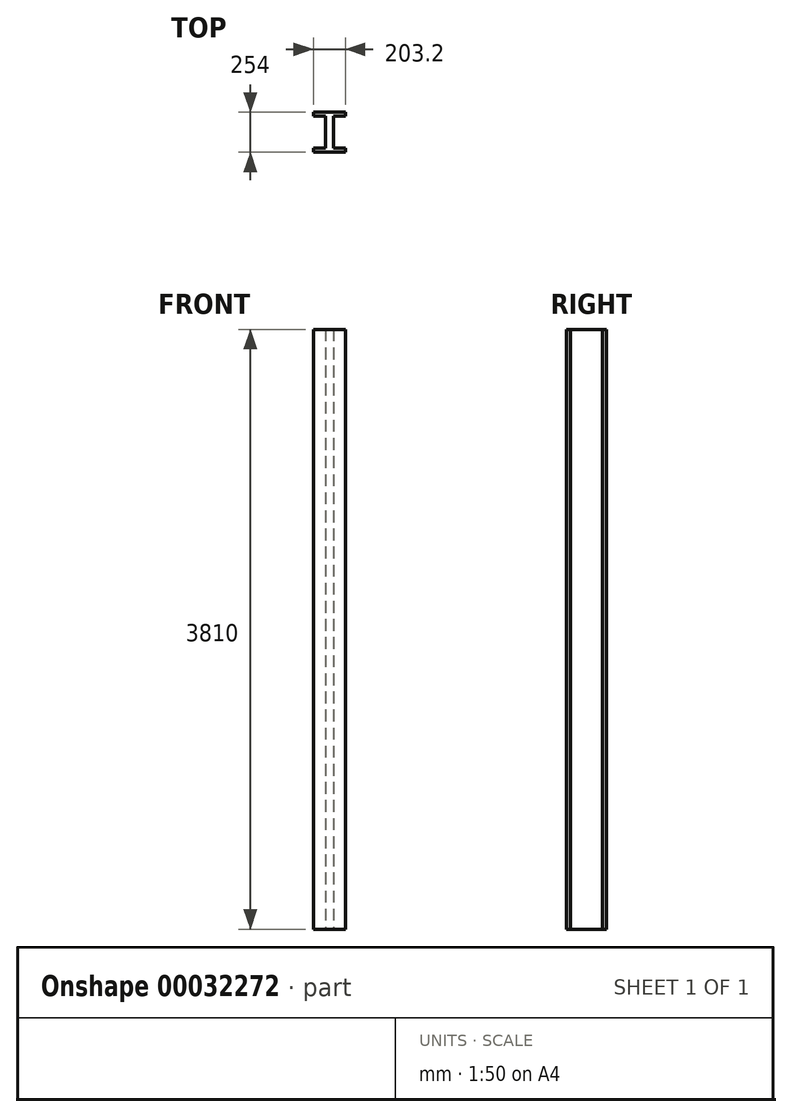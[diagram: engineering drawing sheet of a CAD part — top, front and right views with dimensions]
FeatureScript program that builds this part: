
annotation { "Feature Type Name" : "Feature", "Feature Type Description" : "" }
export const myFeature = defineFeature(function(context is Context, id is Id, definition is map)
    precondition{}
    {
        {
            var Q0;
            Q0=qCreatedBy(makeId("Top.planeOp"),FACE);
            var sketch = newSketch(context, id + "F0", { "sketchPlane" : qUnion([Q0])});
            skLineSegment(sketch, "E0.bottom", {"start": v(0, 0) * mm, "end": v(-203.2, 0) * mm});
            skLineSegment(sketch, "E0.top", {"start": v(0, -254) * mm, "end": v(-203.2, -254) * mm});
            skLineSegment(sketch, "E0.left", {"start": v(0, 0) * mm, "end": v(0, -25.4) * mm});
            skLineSegment(sketch, "E0.right", {"start": v(-203.2, 0) * mm, "end": v(-203.2, -25.4) * mm});
            skLineSegment(sketch, "E1.bottom", {"start": v(-203.2, -25.4) * mm, "end": v(-127, -25.4) * mm});
            skLineSegment(sketch, "E1.top", {"start": v(-203.2, -228.6) * mm, "end": v(-127, -228.6) * mm});
            skLineSegment(sketch, "E1.right", {"start": v(-127, -25.4) * mm, "end": v(-127, -228.6) * mm});
            skLineSegment(sketch, "E2.bottom", {"start": v(0, -25.4) * mm, "end": v(-76.2, -25.4) * mm});
            skLineSegment(sketch, "E2.top", {"start": v(0, -228.6) * mm, "end": v(-76.2, -228.6) * mm});
            skLineSegment(sketch, "E2.right", {"start": v(-76.2, -25.4) * mm, "end": v(-76.2, -228.6) * mm});
            skLineSegment(sketch, "E3.trimOffspring", {"start": v(-203.2, -228.6) * mm, "end": v(-203.2, -254) * mm});
            skLineSegment(sketch, "E4.trimOffspring", {"start": v(0, -228.6) * mm, "end": v(0, -254) * mm});
            skSolve(sketch);
        }
        {
            var Q0;
            Q0=makeQuery(id+"F0.imprint","IMPRINT",FACE,{"disambiguationData":[TD([[makeQuery(id+"F0.imprint","IMPRINT",EDGE,{"derivedFrom":sQuery(id+"F0.wireOp",EDGE,"E0.bottom")}),1.0]])]});
            extrude(context, id + "F1", {"entities" : qUnion([Q0]), "depth" : 3810 * mm});
        }
    });
